# Revit family: Vistafold_Sliding_Folding_5_Standard
name_source: partatom
category: Doors
revit_build: Autodesk Revit 2014 (Build: 20130308_1515(x64)
units: mm (PartAtom-declared; Revit-internal decimal feet)

## types (20) — shared parameters
All Available Glazing Numbers = The rows below list the available glazing materials for this window:
Centered In Wall = Yes
DG Air Gap Thickness = 12 mm  [stored 0.0393701 ft]
DG Thickness Calc = 6 mm  [stored 0.019685 ft]
Description = Sliding folding door, 5 panel
Double Glazing Gasket Material = Double Glazing Gasket Material
Frame Thickness = 75 mm  [stored 0.246063 ft]
Limit Door Height Min = 367 mm  [stored 1.20407 ft]
Limit Door Width Min = 1584 mm  [stored 5.19685 ft]
Limit Sash Height Min = 300 mm  [stored 0.984252 ft]
Limit Sash Width Min = 300 mm  [stored 0.984252 ft]
Manufacturer = Crealco
Max System DG One Piece Thickness = 6 mm  [stored 0.019685 ft]
Max System DG Unit Thickness = 25 mm  [stored 0.082021 ft]
Model = Vistafold
Number Of Sash Inserts = 5
Rough Width = 3 mm  [stored 0.00984252 ft]
Sash Bottom Gap = 33 mm  [stored 0.108268 ft]
Sash Frame Seal = 3 mm  [stored 0.00984252 ft]
Sash Side Gap = 34 mm
Sash Spacing Gap = 4 mm  [stored 0.0131234 ft]
Sash Top Gap = 34 mm
Thickness = 758 mm
URL = http://www.crealco.co.za
Wall Closure = By host
zero-valued in all types: Custom Frame Offset From Exterior, Default Sill Height, IGDB or SAGDB Number

## per-type parameters (varying)
| type | Custom Door Height | Custom Door Width | Custom Windload | Height | Intruderprufe Insulated LowE SHGC Value | Intruderprufe Insulated LowE U Value | Intruderprufe Insulated SHGC Value | Intruderprufe Insulated U Value | Intruderprufe LowE SHGC Value | Intruderprufe LowE U Value | Intruderprufe SHGC Value | Intruderprufe U Value | Limit Door Height Max | Limit Door Width Max | Limit Sash Height Max | Limit Sash Width Max | Max Pane Area | Sash Height | Sash Width | Toughened Safety SHGC Value | Toughened Safety U Value | Width | Windload Design |
| Vistafold-5-1821-1000Pa | 2090 mm  [stored 6.85696 ft] | 1790 mm  [stored 5.8727 ft] | 1000 mm  [stored 3.28084 ft] | 2090 mm  [stored 6.85696 ft] | 0.367 | 4.33 | 0.405 | 4.66 | 0.404 | 5.76 | 0.471 | 6.31 | 2467 mm  [stored 8.09383 ft] | 4584 mm | 2400 mm | 900 mm  [stored 2.95276 ft] | 0.51 m² | 2023 mm  [stored 6.63714 ft] | 341 mm | 0.497 | 6.41 | 1790 mm  [stored 5.8727 ft] | 1000 mm  [stored 3.28084 ft] |
| Vistafold-5-1821-1500Pa | 2090 mm  [stored 6.85696 ft] | 1790 mm  [stored 5.8727 ft] | 1500 mm  [stored 4.92126 ft] | 2090 mm  [stored 6.85696 ft] | 0.367 | 4.33 | 0.405 | 4.66 | 0.404 | 5.76 | 0.471 | 6.31 | 2167 mm | 3084 mm | 2100 mm | 600 mm  [stored 1.9685 ft] | 0.51 m² | 2023 mm  [stored 6.63714 ft] | 341 mm | 0.497 | 6.41 | 1790 mm  [stored 5.8727 ft] | 1500 mm  [stored 4.92126 ft] |
| Vistafold-5-2121-1000Pa | 2090 mm  [stored 6.85696 ft] | 2090 mm  [stored 6.85696 ft] | 1000 mm  [stored 3.28084 ft] | 2090 mm  [stored 6.85696 ft] | 0.396 | 4.06 | 0.437 | 4.44 | 0.438 | 5.52 | 0.508 | 6.25 | 2467 mm  [stored 8.09383 ft] | 4584 mm | 2400 mm | 900 mm  [stored 2.95276 ft] | 0.63 m² | 2023 mm  [stored 6.63714 ft] | 401 mm | 0.536 | 6.35 | 2090 mm  [stored 6.85696 ft] | 1000 mm  [stored 3.28084 ft] |
| Vistafold-5-2121-1500Pa | 2090 mm  [stored 6.85696 ft] | 2090 mm  [stored 6.85696 ft] | 1500 mm  [stored 4.92126 ft] | 2090 mm  [stored 6.85696 ft] | 0.396 | 4.06 | 0.437 | 4.44 | 0.438 | 5.52 | 0.508 | 6.25 | 2167 mm | 3084 mm | 2100 mm | 600 mm  [stored 1.9685 ft] | 0.63 m² | 2023 mm  [stored 6.63714 ft] | 401 mm | 0.536 | 6.35 | 2090 mm  [stored 6.85696 ft] | 1500 mm  [stored 4.92126 ft] |
| Vistafold-5-2421-1000Pa | 2090 mm  [stored 6.85696 ft] | 2390 mm  [stored 7.84121 ft] | 1000 mm  [stored 3.28084 ft] | 2090 mm  [stored 6.85696 ft] | 0.417 | 3.85 | 0.461 | 4.27 | 0.463 | 5.34 | 0.535 | 6.21 | 2467 mm  [stored 8.09383 ft] | 4584 mm | 2400 mm | 900 mm  [stored 2.95276 ft] | 0.75 m² | 2023 mm  [stored 6.63714 ft] | 461 mm | 0.566 | 6.31 | 2390 mm  [stored 7.84121 ft] | 1000 mm  [stored 3.28084 ft] |
| Vistafold-5-2421-1500Pa | 2090 mm  [stored 6.85696 ft] | 2390 mm  [stored 7.84121 ft] | 1500 mm  [stored 4.92126 ft] | 2090 mm  [stored 6.85696 ft] | 0.417 | 3.85 | 0.461 | 4.27 | 0.463 | 5.34 | 0.535 | 6.21 | 2167 mm | 3084 mm | 2100 mm | 600 mm  [stored 1.9685 ft] | 0.75 m² | 2023 mm  [stored 6.63714 ft] | 461 mm | 0.566 | 6.31 | 2390 mm  [stored 7.84121 ft] | 1500 mm  [stored 4.92126 ft] |
| Vistafold-5-2721-1000Pa | 2090 mm  [stored 6.85696 ft] | 2690 mm | 1000 mm  [stored 3.28084 ft] | 2090 mm  [stored 6.85696 ft] | 0.434 | 3.69 | 0.48 | 4.14 | 0.483 | 5.21 | 0.557 | 6.17 | 2467 mm  [stored 8.09383 ft] | 4584 mm | 2400 mm | 900 mm  [stored 2.95276 ft] | 0.86 m² | 2023 mm  [stored 6.63714 ft] | 521 mm | 0.589 | 6.28 | 2690 mm | 1000 mm  [stored 3.28084 ft] |
| Vistafold-5-2721-1500Pa | 2090 mm  [stored 6.85696 ft] | 2690 mm | 1500 mm  [stored 4.92126 ft] | 2090 mm  [stored 6.85696 ft] | 0.434 | 3.69 | 0.48 | 4.14 | 0.483 | 5.21 | 0.557 | 6.17 | 2167 mm | 3084 mm | 2100 mm | 600 mm  [stored 1.9685 ft] | 0.86 m² | 2023 mm  [stored 6.63714 ft] | 521 mm | 0.589 | 6.28 | 2690 mm | 1500 mm  [stored 4.92126 ft] |
| Vistafold-5-3021-1000Pa | 2090 mm  [stored 6.85696 ft] | 2990 mm  [stored 9.80971 ft] | 1000 mm  [stored 3.28084 ft] | 2090 mm  [stored 6.85696 ft] | 0.447 | 3.56 | 0.495 | 4.04 | 0.499 | 5.1 | 0.574 | 6.14 | 2467 mm  [stored 8.09383 ft] | 4584 mm | 2400 mm | 900 mm  [stored 2.95276 ft] | 0.98 m² | 2023 mm  [stored 6.63714 ft] | 581 mm | 0.608 | 6.25 | 2990 mm  [stored 9.80971 ft] | 1000 mm  [stored 3.28084 ft] |
| Vistafold-5-3021-1500Pa | 2090 mm  [stored 6.85696 ft] | 2990 mm  [stored 9.80971 ft] | 1500 mm  [stored 4.92126 ft] | 2090 mm  [stored 6.85696 ft] | 0.447 | 3.56 | 0.495 | 4.04 | 0.499 | 5.1 | 0.574 | 6.14 | 2167 mm | 3084 mm | 2100 mm | 600 mm  [stored 1.9685 ft] | 0.98 m² | 2023 mm  [stored 6.63714 ft] | 581 mm | 0.608 | 6.25 | 2990 mm  [stored 9.80971 ft] | 1500 mm  [stored 4.92126 ft] |
| Vistafold-5-3321-1000Pa | 2090 mm  [stored 6.85696 ft] | 3290 mm | 1000 mm  [stored 3.28084 ft] | 2090 mm  [stored 6.85696 ft] | 0.458 | 3.46 | 0.507 | 3.95 | 0.512 | 5.01 | 0.588 | 6.12 | 2467 mm  [stored 8.09383 ft] | 4584 mm | 2400 mm | 900 mm  [stored 2.95276 ft] | 1.1 m² | 2023 mm  [stored 6.63714 ft] | 641 mm | 0.623 | 6.23 | 3290 mm | 1000 mm  [stored 3.28084 ft] |
| Vistafold-5-3621-1000Pa | 2090 mm  [stored 6.85696 ft] | 3590 mm | 1000 mm  [stored 3.28084 ft] | 2090 mm  [stored 6.85696 ft] | 0.467 | 3.37 | 0.518 | 3.88 | 0.523 | 4.93 | 0.6 | 6.1 | 2467 mm  [stored 8.09383 ft] | 4584 mm | 2400 mm | 900 mm  [stored 2.95276 ft] | 1.21 m² | 2023 mm  [stored 6.63714 ft] | 701 mm | 0.636 | 6.21 | 3590 mm | 1000 mm  [stored 3.28084 ft] |
| Vistafold-5-3921-1000Pa | 2090 mm  [stored 6.85696 ft] | 3890 mm | 1000 mm  [stored 3.28084 ft] | 2090 mm  [stored 6.85696 ft] | 0.475 | 3.3 | 0.526 | 3.83 | 0.532 | 4.87 | 0.61 | 6.08 | 2467 mm  [stored 8.09383 ft] | 4584 mm | 2400 mm | 900 mm  [stored 2.95276 ft] | 1.33 m² | 2023 mm  [stored 6.63714 ft] | 761 mm | 0.646 | 6.19 | 3890 mm | 1000 mm  [stored 3.28084 ft] |
| Vistafold-5-4221-1000Pa | 2090 mm  [stored 6.85696 ft] | 4190 mm | 1000 mm  [stored 3.28084 ft] | 2090 mm  [stored 6.85696 ft] | 0.482 | 3.24 | 0.534 | 3.78 | 0.54 | 4.81 | 0.618 | 6.07 | 2467 mm  [stored 8.09383 ft] | 4584 mm | 2400 mm | 900 mm  [stored 2.95276 ft] | 1.45 m² | 2023 mm  [stored 6.63714 ft] | 821 mm | 0.656 | 6.18 | 4190 mm | 1000 mm  [stored 3.28084 ft] |
| Vistafold-5-4521-1000Pa | 2090 mm  [stored 6.85696 ft] | 4490 mm | 1000 mm  [stored 3.28084 ft] | 2090 mm  [stored 6.85696 ft] | 0.487 | 3.8 | 0.54 | 3.73 | 0.547 | 4.76 | 0.626 | 6.06 | 2467 mm  [stored 8.09383 ft] | 4584 mm | 2400 mm | 900 mm  [stored 2.95276 ft] | 1.56 m² | 2023 mm  [stored 6.63714 ft] | 881 mm | 0.664 | 6.17 | 4490 mm | 1000 mm  [stored 3.28084 ft] |
| Vistafold-5-1824-1000Pa | 2390 mm  [stored 7.84121 ft] | 1790 mm  [stored 5.8727 ft] | 1000 mm  [stored 3.28084 ft] | 2390 mm  [stored 7.84121 ft] | 0.371 | 4.3 | 0.41 | 4.63 | 0.408 | 5.74 | 0.476 | 6.31 | 2467 mm  [stored 8.09383 ft] | 3084 mm | 2400 mm | 600 mm  [stored 1.9685 ft] | 0.59 m² | 2323 mm | 341 mm | 0.502 | 6.4 | 1790 mm  [stored 5.8727 ft] | 1000 mm  [stored 3.28084 ft] |
| Vistafold-5-2124-1000Pa | 2390 mm  [stored 7.84121 ft] | 2090 mm  [stored 6.85696 ft] | 1000 mm  [stored 3.28084 ft] | 2390 mm  [stored 7.84121 ft] | 0.4 | 4.02 | 0.442 | 4.4 | 0.443 | 5.5 | 0.514 | 6.31 | 2467 mm  [stored 8.09383 ft] | 3084 mm | 2400 mm | 600 mm  [stored 1.9685 ft] | 0.73 m² | 2323 mm | 401 mm | 0.543 | 6.34 | 2090 mm  [stored 6.85696 ft] | 1000 mm  [stored 3.28084 ft] |
| Vistafold-5-2424-1000Pa | 2390 mm  [stored 7.84121 ft] | 2390 mm  [stored 7.84121 ft] | 1000 mm  [stored 3.28084 ft] | 2390 mm  [stored 7.84121 ft] | 0.422 | 3.81 | 0.467 | 4.23 | 0.469 | 5.31 | 0.542 | 6.2 | 2467 mm  [stored 8.09383 ft] | 3084 mm | 2400 mm | 600 mm  [stored 1.9685 ft] | 0.86 m² | 2323 mm | 461 mm | 0.573 | 6.3 | 2390 mm  [stored 7.84121 ft] | 1000 mm  [stored 3.28084 ft] |
| Vistafold-5-2724-1000Pa | 2390 mm  [stored 7.84121 ft] | 2690 mm | 1000 mm  [stored 3.28084 ft] | 2390 mm  [stored 7.84121 ft] | 0.439 | 3.65 | 0.486 | 4.1 | 0.489 | 5.17 | 0.564 | 6.16 | 2467 mm  [stored 8.09383 ft] | 3084 mm | 2400 mm | 600 mm  [stored 1.9685 ft] | 1 m² | 2323 mm | 521 mm | 0.597 | 6.27 | 2690 mm | 1000 mm  [stored 3.28084 ft] |
| Vistafold-5-3024-1000Pa | 2390 mm  [stored 7.84121 ft] | 2990 mm  [stored 9.80971 ft] | 1000 mm  [stored 3.28084 ft] | 2390 mm  [stored 7.84121 ft] | 0.453 | 3.52 | 0.501 | 4 | 0.505 | 5.06 | 0.581 | 6.13 | 2467 mm  [stored 8.09383 ft] | 3084 mm | 2400 mm | 600 mm  [stored 1.9685 ft] | 1.13 m² | 2323 mm | 581 mm | 0.615 | 6.24 | 2990 mm  [stored 9.80971 ft] | 1000 mm  [stored 3.28084 ft] |

note: [stored X ft] marks values corroborated as IEEE doubles in the binary element streams (Revit-internal decimal feet)

## geometry (parser evidence)
native form markers: Sweep x27
no freeform markers — native parametric forms only
